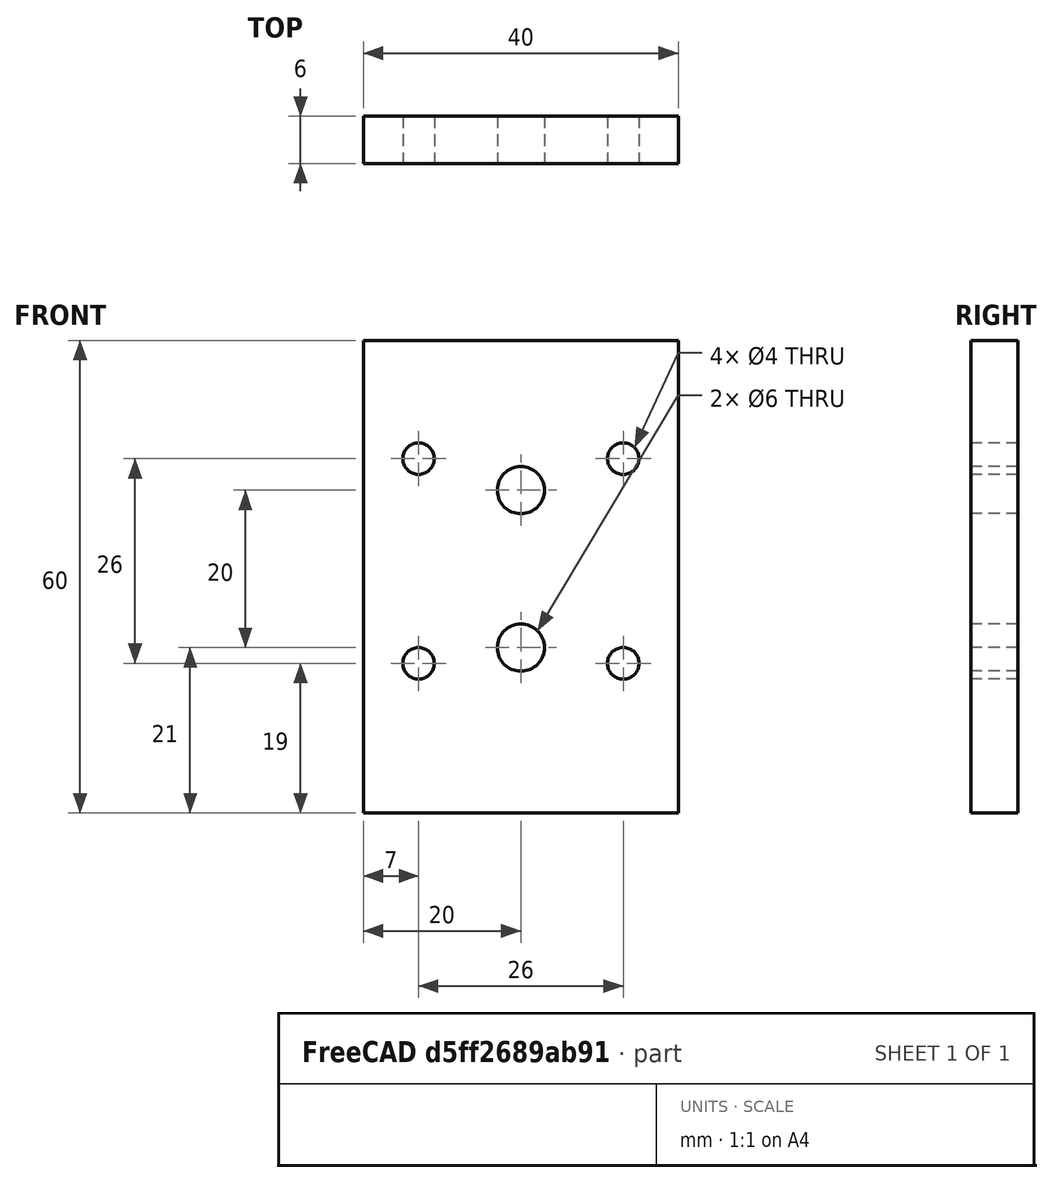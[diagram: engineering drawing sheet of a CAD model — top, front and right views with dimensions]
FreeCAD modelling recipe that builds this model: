
FCSTD DOCUMENT  (FreeCAD 0.15R4671 (Git))
Label: soporte brazo guia lineal
License: All rights reserved
LicenseURL: http://es.wikipedia.org/wiki/Todos_los_derechos_reservados
objects: Part::Cylinder×2, Part::FeaturePython×2, Part::Cut×2, App::MeasureDistance×2, Part::Box×1
note: 7 computed .brp shape members not serialized (recipe doc carries the construction recipe); baked Part::Feature solids carry a one-line shape summary decoded from their .brp

FEATURE [Part::Box] Box  label="Cubo"
  Height = 6
  Length = 40
  Placement = pos=(0,0,0) rot=(1,0,0;1.5708rad)
  Width = 60
FEATURE [Part::Cylinder] Cylinder  label="Cilindro"
  Angle = 360
  Height = 6
  Placement = pos=(7,0,19) rot=(1,0,0;1.5708rad)
  Radius = 2
FEATURE [Part::FeaturePython] Array  # Draft array (typed FeaturePython)
  Angle = 360
  ArrayType = 0
  Axis = (0,0,1)
  Base = -> Cylinder
  Center = (0,0,0)
  Fuse = false
  IntervalAxis = (0,0,0)
  IntervalX = (26,0,0)
  IntervalY = (0,0,0)
  IntervalZ = (0,0,26)
  NumberPolar = 1
  NumberX = 2
  NumberY = 1
  NumberZ = 2
FEATURE [Part::Cut] Cut
  Base = -> Box
  Tool = -> Array
FEATURE [App::MeasureDistance] Distance  label="Distance: 18.008"
  Distance = 18.0079
  P1 = (32.1256,0,39.0039)
  P2 = (32.1256,0,20.9961)
FEATURE [App::MeasureDistance] Distance001  label="Distance: 25.973"
  Distance = 25.9733
  P1 = (32.6252,0,46.9646)
  P2 = (33.1256,0,20.9961)
FEATURE [Part::Cylinder] Cylinder001  label="Cilindro001"
  Angle = 360
  Height = 10
  Placement = pos=(20,0,21) rot=(1,0,0;1.5708rad)
  Radius = 3
FEATURE [Part::FeaturePython] Array001  # Draft array (typed FeaturePython)
  Angle = 360
  ArrayType = 0
  Axis = (0,0,1)
  Base = -> Cylinder001
  Center = (0,0,0)
  Fuse = false
  IntervalAxis = (0,0,0)
  IntervalX = (1,0,0)
  IntervalY = (0,1,0)
  IntervalZ = (0,0,20)
  NumberPolar = 1
  NumberX = 1
  NumberY = 1
  NumberZ = 2
FEATURE [Part::Cut] Cut001
  Base = -> Cut
  Tool = -> Array001
